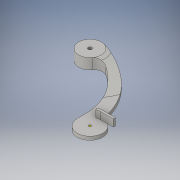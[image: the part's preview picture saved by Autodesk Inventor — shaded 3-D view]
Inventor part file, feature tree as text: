
AUTODESK INVENTOR PART (.ipt)
format: ipt  version: 2016 (Build 200138000, 138)  size: 277,504 bytes
history: native  units: in
note: dims shown in document units (in); Inventor stores cm internally (conversion verified against a paired STEP export)
features: sketch x18, extrude x16, fillet x4, mirror x1, chamfer x1
ambient origin geometry x8: Origin, YZ Plane, XZ Plane, XY Plane, X Axis, Y Axis, Z Axis, Center Point
bodies: Solid1 (feature_tree)
feature tree (40):
  extrude  "Extrusion1"  Depth=0.75in
  extrude  "Extrusion2"  Depth=0.25in TaperAngle=0.0deg
  extrude  "Extrusion3"  Depth=0.3125in TaperAngle=0.0deg
  extrude  "Extrusion6"  Depth=0.25in TaperAngle=0.0deg
  extrude  "Extrusion7"  Depth=0.25in TaperAngle=0.0deg
  extrude  "Extrusion8"  Depth=0.25in TaperAngle=0.0deg
  extrude  "Extrusion9"  TaperAngle=135.0deg  [1 undecoded]
  extrude  "Extrusion13"  Depth=0.6918in
  fillet  "Fillet3"  Radius=0.1299in
  fillet  "Fillet4"  Radius=0.1299in
  fillet  "Fillet5"  Radius=0.125in
  mirror  "Mirror1"
  extrude  "Extrusion14"  Depth=0.3in
  extrude  "Extrusion15"  Depth=0.125in TaperAngle=0.0deg
  extrude  "Extrusion16"  Depth=0.125in TaperAngle=0.0deg
  extrude  "Extrusion17"  Depth=0.125in TaperAngle=0.0deg
  sketch  "Sketch18"  dims[d66=0.125in d67=0.0in d68=0.125in d69=0.0in]
  extrude  "Extrusion18"  Depth=0.125in TaperAngle=0.0deg
  extrude  "Extrusion19"  Depth=0.25in TaperAngle=45.0deg
  extrude  "Extrusion20"  [1 undecoded]
  sketch  "Sketch22"
  extrude  "Extrusion21"  [1 undecoded]
  chamfer  "Chamfer1"  [1 undecoded]
  fillet  "Fillet6"  [1 undecoded]
  sketch  "Sketch1"  dims[d0=0.9in d1=0.75in]
  sketch  "Sketch2"  dims[d2=0.25in d3=0.0in d4=0.125in d5=0.0in]
  sketch  "Sketch3"  dims[d6=0.0866in d7=0.3125in d8=0.0in]
  sketch  "Sketch6"  dims[d14=0.25in d15=0.0in d16=0.45in d17=0.0in]
  sketch  "Sketch7"  dims[d18=135.0deg d19=0.25in d20=0.0in]
  sketch  "Sketch8"  dims[d21=112.5deg d22=0.25in d23=0.0in]
  sketch  "Sketch9"  dims[d44=3.0in d45=135.0deg]
  sketch  "Sketch13"  dims[d46=0.8in d47=0.6918in d48=0.1299in d49=0.1299in d50=0.125in d51=0.0in]
  sketch  "Sketch14"  dims[d52=2.0in d53=0.3in]
  sketch  "Sketch15"  dims[d54=2.5in d55=0.125in d56=0.0in]
  sketch  "Sketch16"  dims[d57=1.0625in d58=0.0in d59=0.125in d60=0.0in]
  sketch  "Sketch17"  dims[d61=0.125in d62=0.0in d63=0.125in d64=0.0in]
  sketch  "Sketch19"  dims[d70=0.25in d71=0.0in d72=0.75in d73=0.25in d74=45.0deg]
  sketch  "Sketch20"  dims[d75=4.0in]
  sketch  "Sketch21"
  sketch  "Sketch23"
note: 5 required parameter values undecoded (feature->parameter linkage not recoverable at this tier; creation-order binding heuristic only, values carry confidence <= 0.55)
